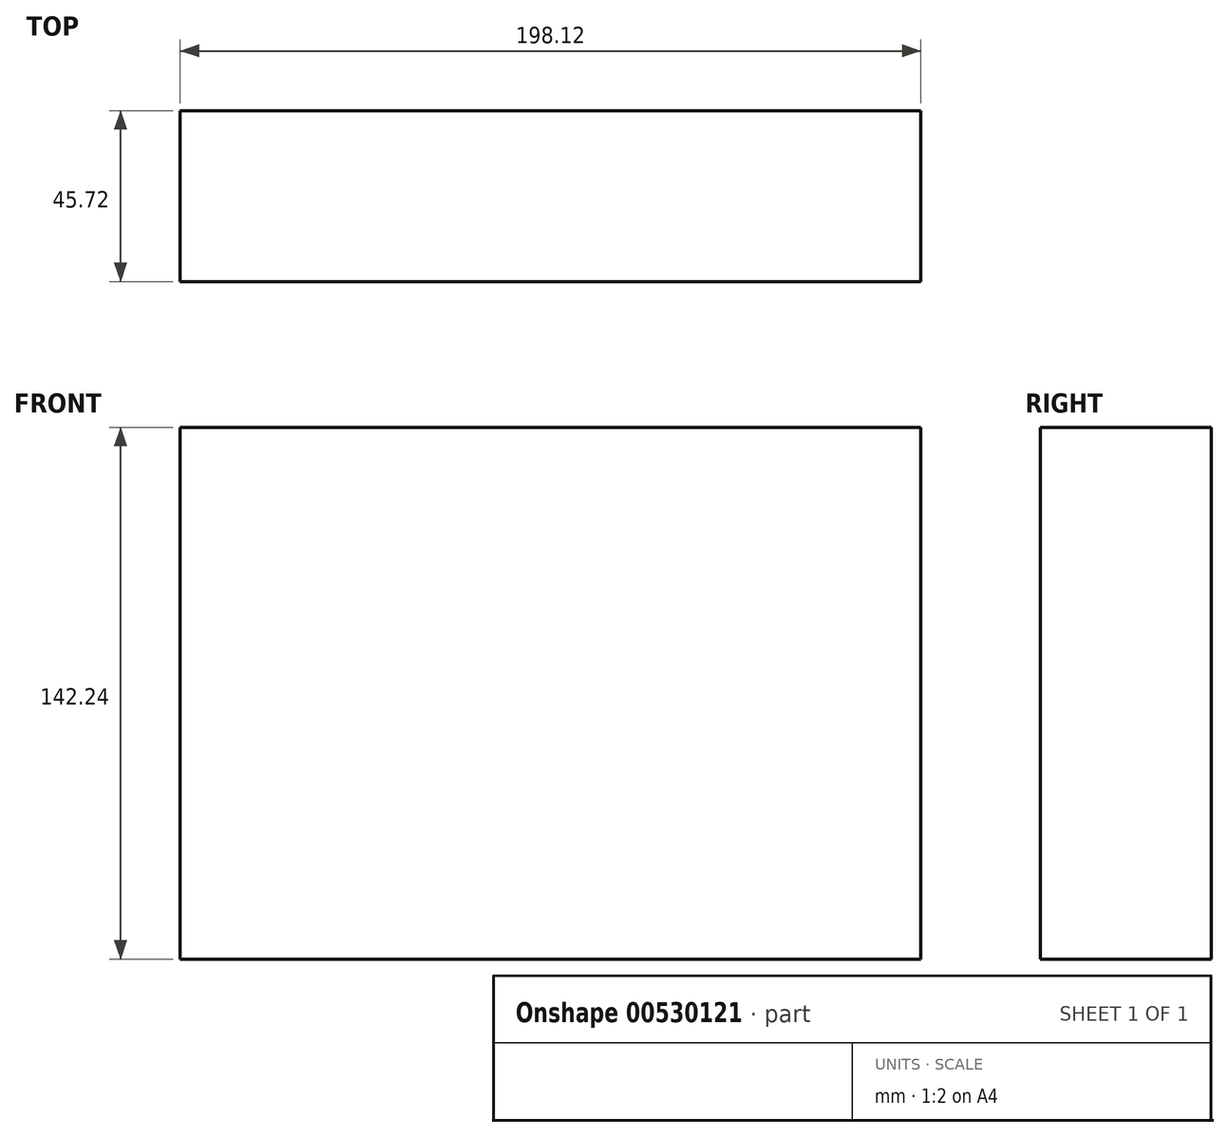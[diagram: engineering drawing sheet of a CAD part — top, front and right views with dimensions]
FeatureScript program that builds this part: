
annotation { "Feature Type Name" : "Feature", "Feature Type Description" : "" }
export const myFeature = defineFeature(function(context is Context, id is Id, definition is map)
    precondition{}
    {
        {
            var Q0;
            Q0=qCreatedBy(makeId("Front.planeOp"),FACE);
            var sketch = newSketch(context, id + "F0", { "sketchPlane" : qUnion([Q0])});
            skLineSegment(sketch, "E0.bottom", {"start": v(-99.06, 71.12) * mm, "end": v(99.06, 71.12) * mm});
            skLineSegment(sketch, "E0.top", {"start": v(-99.06, -71.12) * mm, "end": v(99.06, -71.12) * mm});
            skLineSegment(sketch, "E0.left", {"start": v(-99.06, 71.12) * mm, "end": v(-99.06, -71.12) * mm});
            skLineSegment(sketch, "E0.right", {"start": v(99.06, 71.12) * mm, "end": v(99.06, -71.12) * mm});
            skPoint(sketch, "E0.middle", {"position": v(0, 0) * mm});
            skSolve(sketch);
        }
        {
            var Q0;
            Q0 = qSketchRegion(id + "F0", true);
            extrude(context, id + "F1", {"entities" : qUnion([Q0]), "depth" : 45.72 * mm, "offsetDistance" : 25.4 * mm});
        }
    });
